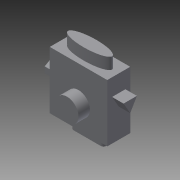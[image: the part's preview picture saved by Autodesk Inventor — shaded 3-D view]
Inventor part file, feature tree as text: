
AUTODESK INVENTOR PART (.ipt)
format: ipt  version: 2015 SP2 (Build 190223200, 223)  size: 137,216 bytes
history: native  units: mm
features: extrude x7, other x7
ambient origin geometry x8: Origin, YZ Plane, XZ Plane, XY Plane, X Axis, Y Axis, Z Axis, Center Point
bodies: Volumenkörper1 (feature_tree)
feature tree (14):
  extrude  "Extrusion1"  Depth=5.0mm
  extrude  "Extrusion2"  Depth=10.0mm
  extrude  "Extrusion3"  Depth=4.0mm
  extrude  "Extrusion4"  Depth=2.0mm
  extrude  "Extrusion5"  Depth=10.0mm TaperAngle=0.0deg
  other  "Ellipse"
  extrude  "Extrusion7"  Depth=4.0mm
  extrude  "Extrusion8"  Depth=2.0mm TaperAngle=0.0deg
  other  "Rechteck"
  other  "Kreis"
  other  "Dreieck"
  other  "Pentagon"
  other  "Hexagon"
  other  "Nase"
